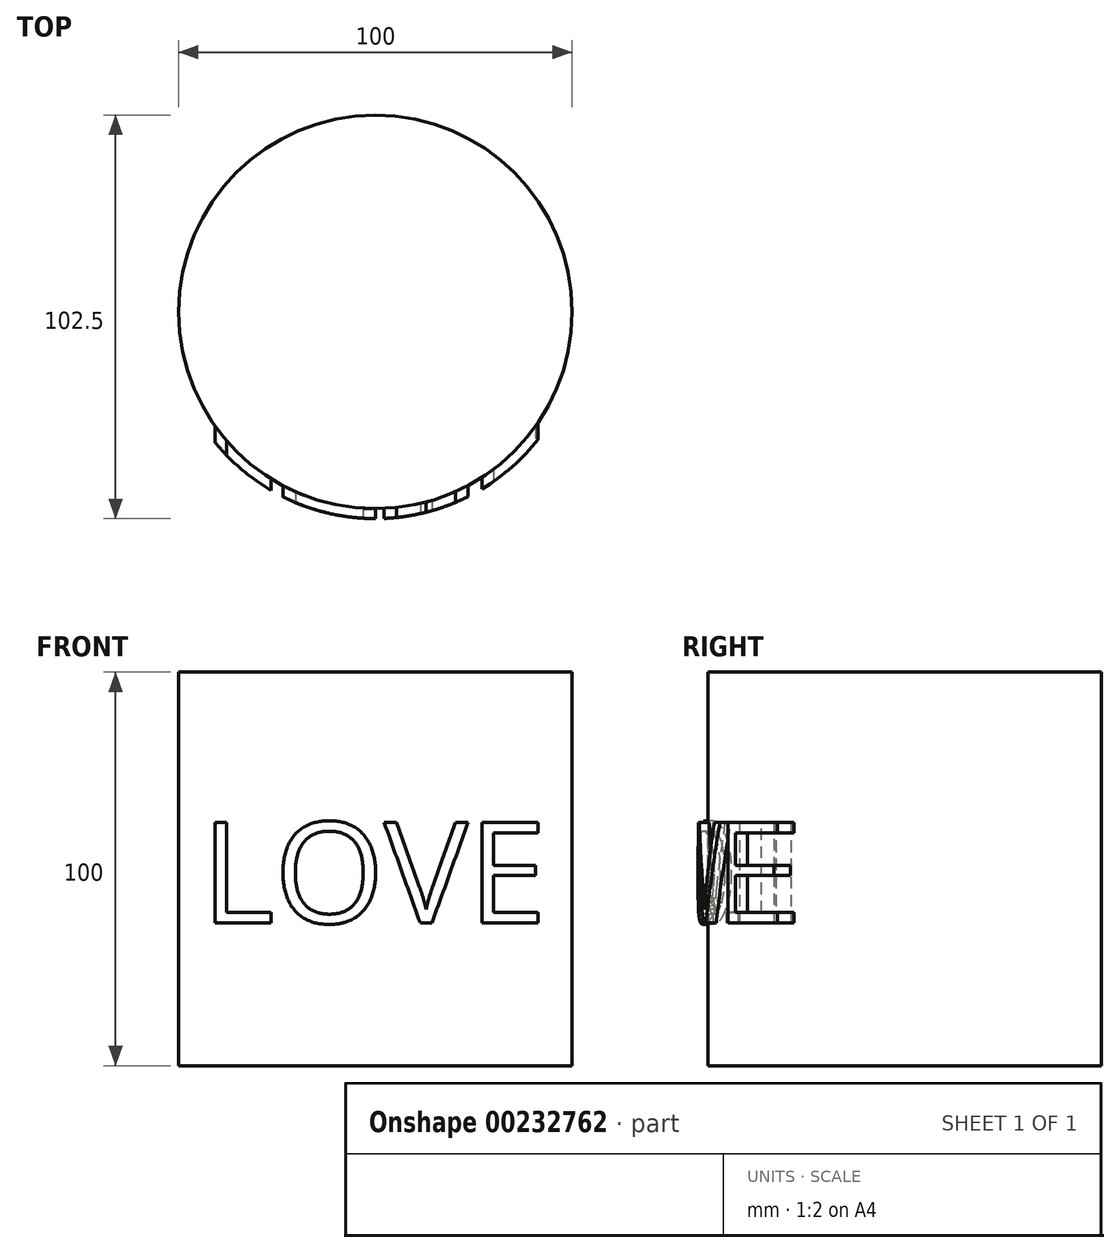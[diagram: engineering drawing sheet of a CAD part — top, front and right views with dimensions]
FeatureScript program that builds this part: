
annotation { "Feature Type Name" : "Feature", "Feature Type Description" : "" }
export const myFeature = defineFeature(function(context is Context, id is Id, definition is map)
    precondition{}
    {
        {
            var Q0;
            Q0=qCreatedBy(makeId("Top.planeOp"),FACE);
            var sketch = newSketch(context, id + "F0", { "sketchPlane" : qUnion([Q0])});
            skCircle(sketch, "E0", {"center": v(0, 0) * mm, "radius": 50 * mm});
            skSolve(sketch);
        }
        {
            var Q0;
            Q0=makeQuery(id+"F0.imprint","IMPRINT",FACE,{"disambiguationData":[TD([[makeQuery(id+"F0.imprint","IMPRINT",EDGE,{"derivedFrom":sQuery(id+"F0.wireOp",EDGE,"E0")}),1.0]])]});
            extrude(context, id + "F1", {"entities" : qUnion([Q0]), "depth" : 100 * mm});
        }
        {
            var Q0;
            Q0=qCreatedBy(makeId("Front.planeOp"),FACE);
            cPlane(context, id + "F2", {"entities" : qUnion([Q0]), "cplaneType" : CPlaneType.OFFSET, "offset" : 70 * mm, "width" : 150 * mm, "height" : 150 * mm});
        }
        {
            var Q0;
            Q0=qCreatedBy(id+"F2.planeOp",FACE);
            var sketch = newSketch(context, id + "F3", { "sketchPlane" : qUnion([Q0])});
            skText(sketch, "E1", { "text": "LOVE", "fontName": "OpenSans-Regular.ttf"});
            const initialGuessF3  = {"E1": [-0.04427, 0.03623, 1, 0, 0.0258]};
            skSetInitialGuess(sketch, initialGuessF3);
            skSolve(sketch);
        }
        {
            var Q0;
            Q0 = qSketchRegion(id + "F3", true);
            extrude(context, id + "F4", {"entities" : qUnion([Q0]), "operationType" : NewBodyOperationType.ADD, "oppositeDirection" : true, "depth" : 46 * mm});
        }
        {
            var Q0;
            Q0=makeQuery(id+"F1.opExtrude","CAP_FACE",FACE,{"disambiguationData":[OSD([sQuery(id+"F0.wireOp",EDGE,"E0")])],"isStart":false});
            var sketch = newSketch(context, id + "F5", { "sketchPlane" : qUnion([Q0])});
            skCircle(sketch, "E2", {"center": v(0, 0) * mm, "radius": 52.5 * mm});
            skCircle(sketch, "E3", {"center": v(0, 0) * mm, "radius": 85.81 * mm});
            skSolve(sketch);
        }
        {
            var Q0;
            Q0=makeQuery(id+"F5.imprint","IMPRINT",FACE,{"disambiguationData":[TD([[makeQuery(id+"F5.imprint","IMPRINT",EDGE,{"derivedFrom":sQuery(id+"F5.wireOp",EDGE,"E2")}),-1.0]])]});
            extrude(context, id + "F6", {"entities" : qUnion([Q0]), "operationType" : NewBodyOperationType.REMOVE, "oppositeDirection" : true, "depth" : 104.3 * mm});
        }
    });
